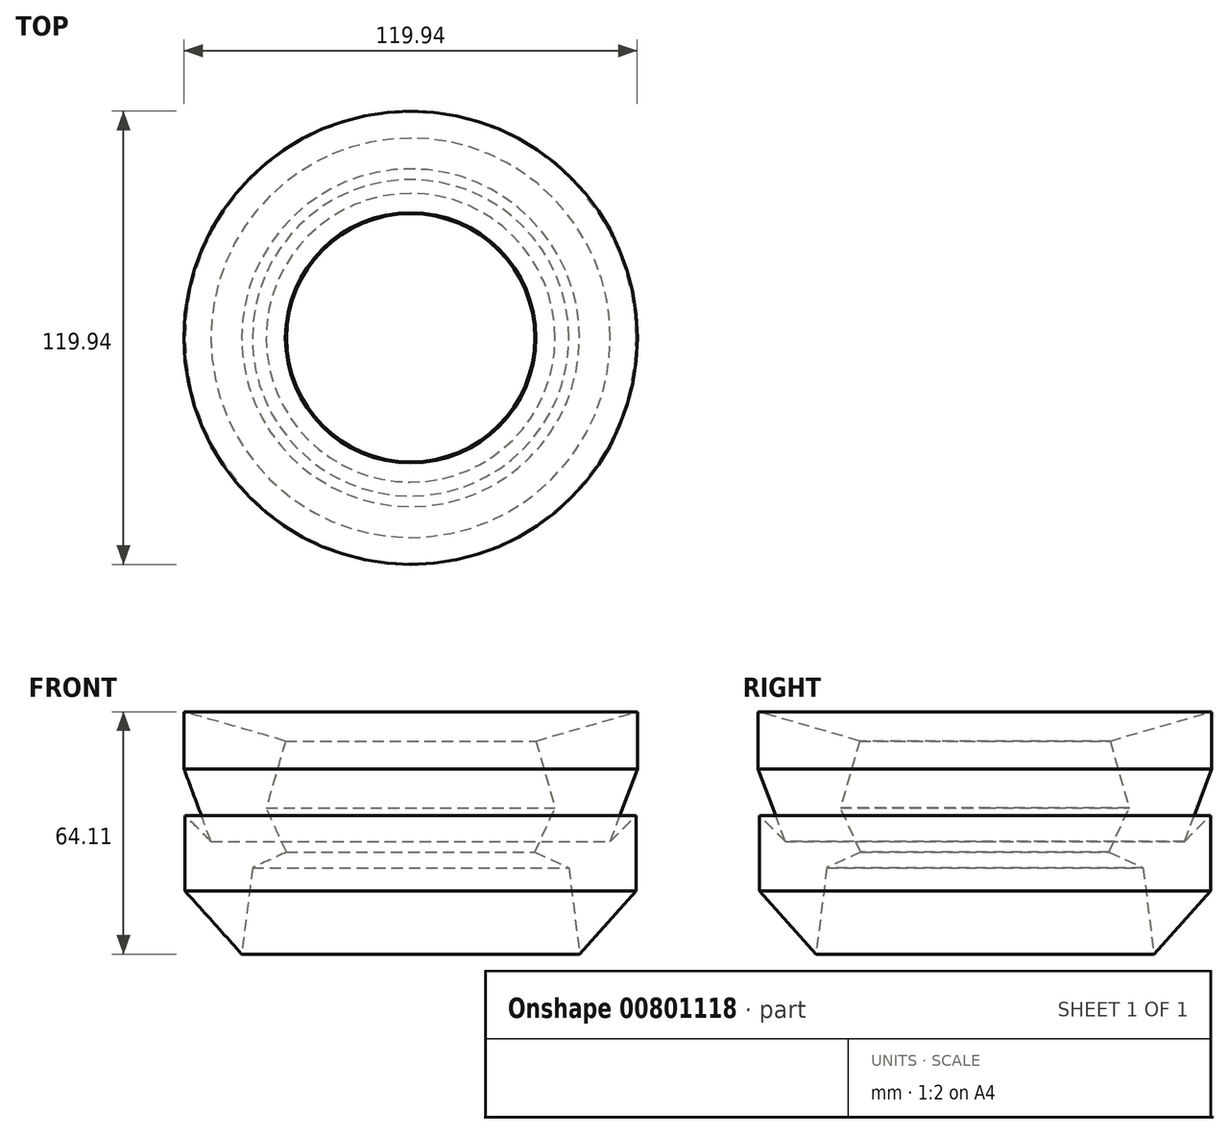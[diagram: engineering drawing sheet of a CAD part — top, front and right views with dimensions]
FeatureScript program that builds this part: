
annotation { "Feature Type Name" : "Feature", "Feature Type Description" : "" }
export const myFeature = defineFeature(function(context is Context, id is Id, definition is map)
    precondition{}
    {
        {
            var Q0;
            Q0=qCreatedBy(makeId("Front.planeOp"),FACE);
            var sketch = newSketch(context, id + "F0", { "sketchPlane" : qUnion([Q0])});
            skLineSegment(sketch, "E0", {"start": v(0, 0) * mm, "end": v(-15, 16.7) * mm});
            skLineSegment(sketch, "E1", {"start": v(-15, 16.7) * mm, "end": v(-15, 36.7) * mm});
            skLineSegment(sketch, "E2", {"start": v(-15, 36.7) * mm, "end": v(-8.14, 29.84) * mm});
            skLineSegment(sketch, "E3", {"start": v(-8.14, 29.84) * mm, "end": v(-15.28, 48.98) * mm});
            skLineSegment(sketch, "E4", {"start": v(-15.28, 48.98) * mm, "end": v(-15.28, 64.11) * mm});
            skLineSegment(sketch, "E5", {"start": v(-15.28, 64.11) * mm, "end": v(11.57, 56.4) * mm});
            skLineSegment(sketch, "E6", {"start": v(11.57, 56.4) * mm, "end": v(6.48, 38.68) * mm});
            skLineSegment(sketch, "E7", {"start": v(6.48, 38.68) * mm, "end": v(11.85, 26.99) * mm});
            skLineSegment(sketch, "E8", {"start": v(11.85, 26.99) * mm, "end": v(2.83, 22.84) * mm});
            skLineSegment(sketch, "E9", {"start": v(2.83, 22.84) * mm, "end": v(0, 0) * mm});
            skLineSegment(sketch, "E10", {"start": v(44.7, 0) * mm, "end": v(44.7, 64.11) * mm});
            skSolve(sketch);
        }
        {
            var Q0;
            Q0=makeQuery(id+"F0.imprint","IMPRINT",FACE,{"disambiguationData":[TD([[makeQuery(id+"F0.imprint","IMPRINT",EDGE,{"derivedFrom":sQuery(id+"F0.wireOp",EDGE,"E0")}),-1.0]])]});
            var Q1;
            Q1=sQuery(id+"F0.wireOp",EDGE,"E10");
            revolve(context, id + "F1", {"surfaceOperationType" : NewSurfaceOperationType.NEW, "entities" : qUnion([Q0]), "axis" : qUnion([Q1]), "revolveType" : RevolveType.FULL});
        }
    });
